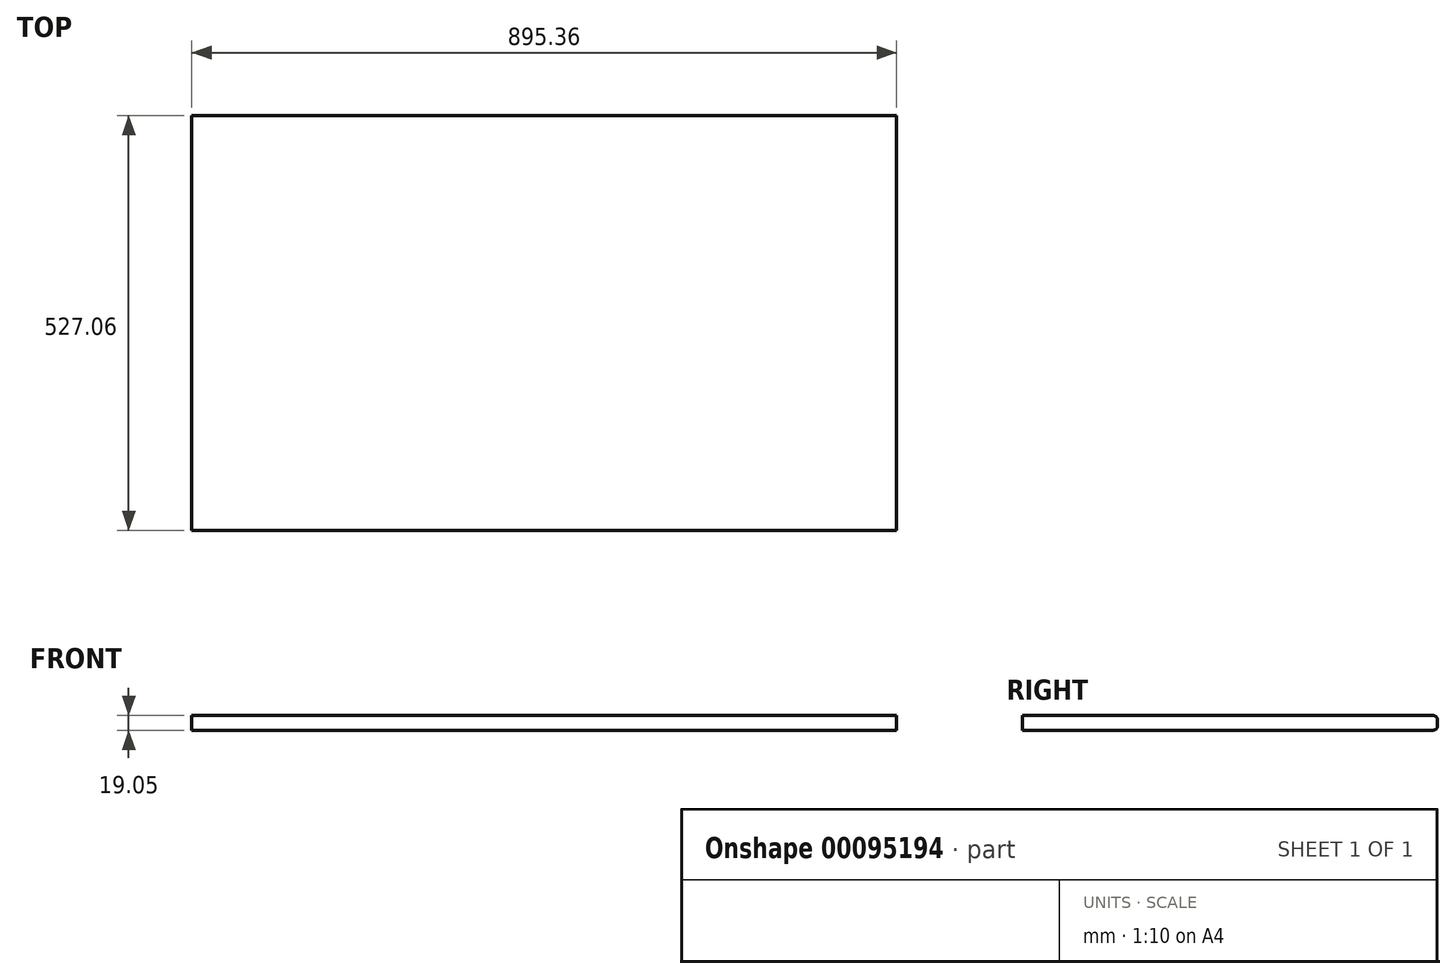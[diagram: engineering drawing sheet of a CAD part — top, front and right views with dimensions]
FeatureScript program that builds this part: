
annotation { "Feature Type Name" : "Feature", "Feature Type Description" : "" }
export const myFeature = defineFeature(function(context is Context, id is Id, definition is map)
    precondition{}
    {
        {
            var Q0;
            Q0=qCreatedBy(makeId("Top.planeOp"),FACE);
            var sketch = newSketch(context, id + "F0", { "sketchPlane" : qUnion([Q0])});
            skLineSegment(sketch, "E0.bottom", {"start": v(447.68, -263.52) * mm, "end": v(-447.68, -263.53) * mm});
            skLineSegment(sketch, "E0.top", {"start": v(447.68, 263.53) * mm, "end": v(-447.68, 263.53) * mm});
            skLineSegment(sketch, "E0.left", {"start": v(447.68, -263.52) * mm, "end": v(447.68, 263.53) * mm});
            skLineSegment(sketch, "E0.right", {"start": v(-447.68, -263.53) * mm, "end": v(-447.68, 263.53) * mm});
            skPoint(sketch, "E0.middle", {"position": v(0, 0) * mm});
            skSolve(sketch);
        }
        {
            var Q0;
            Q0=makeQuery(id+"F0.imprint","IMPRINT",FACE,{"disambiguationData":[TD([[makeQuery(id+"F0.imprint","IMPRINT",EDGE,{"derivedFrom":sQuery(id+"F0.wireOp",EDGE,"E0.bottom")}),-1.0]])]});
            extrude(context, id + "F1", {"entities" : qUnion([Q0]), "depth" : 19.05 * mm});
        }
        {
            var Q0;
            Q0=makeQuery(id+"F1.opExtrude","CAP_EDGE",EDGE,{"disambiguationData":[OSD([sQuery(id+"F0.wireOp",EDGE,"E0.top")])],"isStart":false});
            var Q1;
            Q1=makeQuery(id+"F1.opExtrude","CAP_EDGE",EDGE,{"disambiguationData":[OSD([sQuery(id+"F0.wireOp",EDGE,"E0.top")])],"isStart":true});
            fillet(context, id + "F2", {"entities" : qUnion([Q0, Q1]), "radius" : 6.35 * mm, "tangentPropagation" : true, "allowEdgeOverflow" : false});
        }
    });
